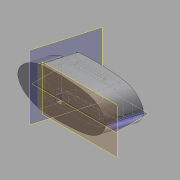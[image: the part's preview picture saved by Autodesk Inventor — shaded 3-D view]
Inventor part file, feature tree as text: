
AUTODESK INVENTOR PART (.ipt)
format: ipt  version: 2012 SP2 (Build 160219200, 219)  size: 445,952 bytes
history: native  units: in
note: dims shown in document units (in); Inventor stores cm internally (conversion verified against a paired STEP export)
features: sketch x13, sweep x5, plane x4, other x2, extrude x1, mirror x1, fillet x1, chamfer x1, surface_op x1
ambient origin geometry x8: Origin, YZ Plane, XZ Plane, XY Plane, X Axis, Y Axis, Z Axis, Center Point
bodies: Solid1 (feature_tree)
feature tree (29):
  sketch  "Sketch1"  dims[d6=0.9405in d9=0.688in]
  plane  "Work Plane1"
  plane  "Work Plane2"
  sketch  "Sketch3"  dims[d12=0.2381in d13=0.5734in]
  plane  "Work Plane3"
  sweep  "Sweep1"
  sweep  "Sweep2"
  extrude  "Extrusion1"  Depth=0.5734in
  plane  "Work Plane4"
  mirror  "Mirror1"
  sweep  "Sweep3"
  sweep  "Sweep5"
  sweep  "Sweep6"
  fillet  "Fillet1"  Radius=0.3395in
  chamfer  "Chamfer1"  Distance=0.323in
  other  "Image1"
  sketch  "Sketch2"  dims[d10=0.069in d11=0.12in]
  other  "Srf1"
  sketch  "Sketch4"  dims[d14=0.4256in d15=1.588in]
  sketch  "Sketch5"  dims[d16=0.3503in d17=0.5806in]
  sketch  "Sketch6"  dims[d18=0.3426in d19=0.2058in d20=0.3395in]
  sketch  "Sketch7"  dims[d21=0.7769in]
  sketch  "Sketch8"  dims[d22=0.3374in]
  sketch  "Sketch9"  dims[d23=0.1206in]
  sketch  "Sketch10"  dims[d24=0.3329in]
  sketch  "Sketch14"  dims[d25=0.8673in]
  sketch  "Sketch15"  dims[d26=0.3313in]
  sketch  "Sketch16"  dims[d27=0.0621in d28=0.323in d29=0.9887in d30=0.2944in d31=1.1563in d32=0.2583in d33=1.2792in d34=0.1988in d35=1.391in d36=0.1269in d37=1.4752in d38=0.0171in d39=1.5524in d40=0.0519in d41=1.5805in d42=0.1042in d43=1.7561in d44=0.2965in d47=0.5902in d48=0.2in d49=0.0in d50=0.6495in d51=1.035in d52=0.5105in d53=0.306in d54=0.5955in d55=0.0in d56=0.6605in d57=0.053in d58=0.1095in d59=0.2in d60=0.055in d61=0.0in d62=0.7687in d64=0.3167in d65=0.4475in d66=0.0in d67=0.0285in d68=0.0285in d69=0.0285in d70=0.0285in d71=0.0285in d72=0.0285in d76=0.0in d77=0.0in d78=0.5in d79=0.08in d80=0.0285in d81=15.0deg]
  surface_op  "Boundary Patch1"
